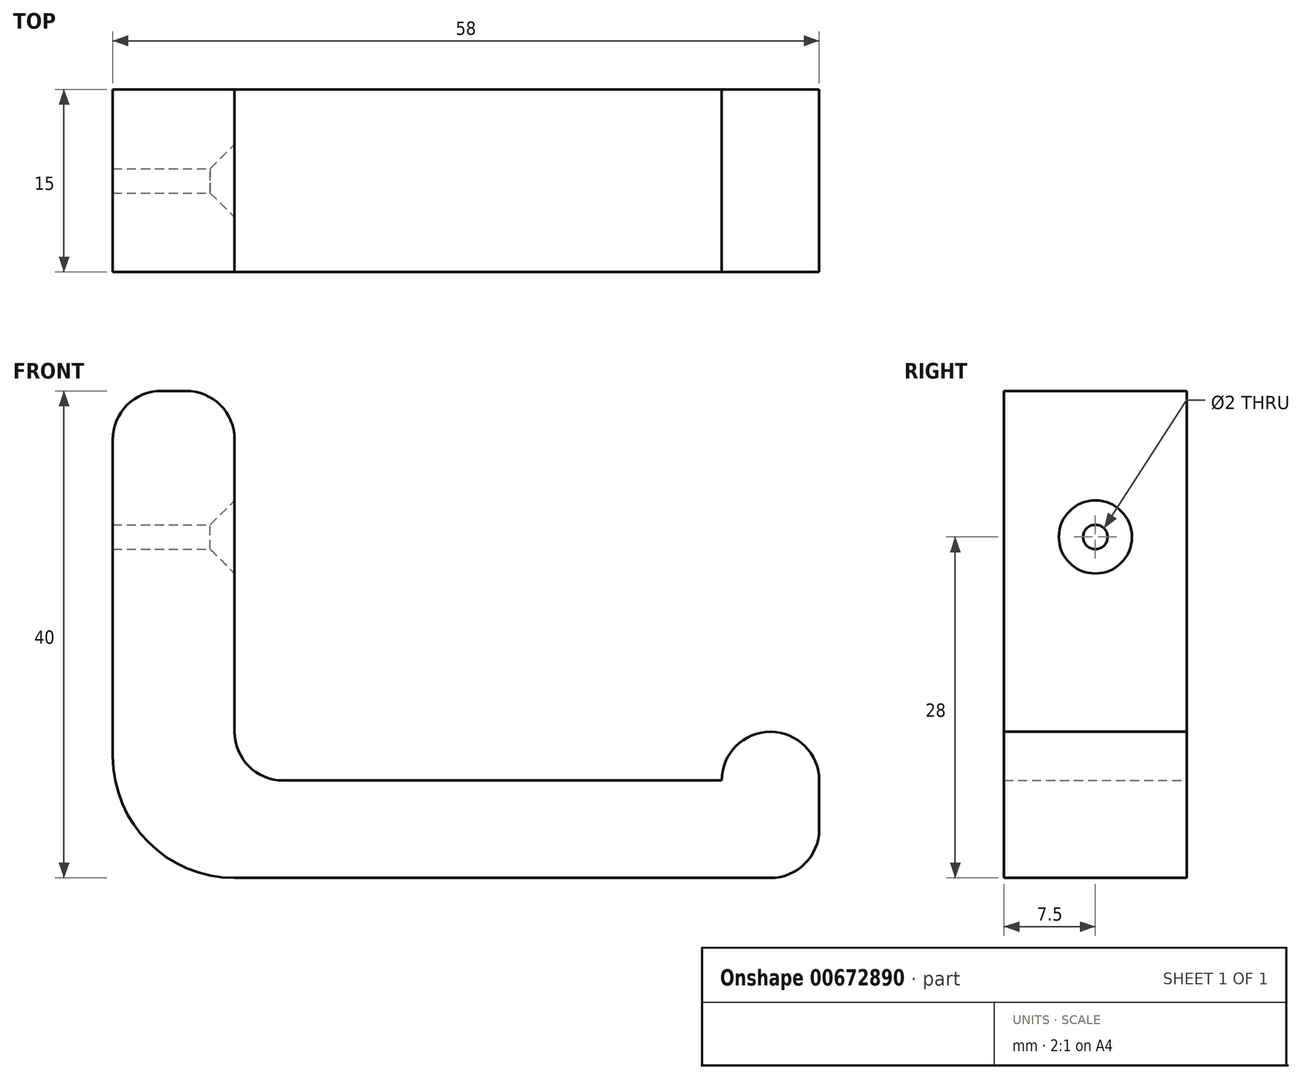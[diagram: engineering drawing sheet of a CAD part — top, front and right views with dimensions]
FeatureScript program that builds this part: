
annotation { "Feature Type Name" : "Feature", "Feature Type Description" : "" }
export const myFeature = defineFeature(function(context is Context, id is Id, definition is map)
    precondition{}
    {
        {
            var Q0;
            Q0=qCreatedBy(makeId("Front.planeOp"),FACE);
            var sketch = newSketch(context, id + "F0", { "sketchPlane" : qUnion([Q0])});
            skLineSegment(sketch, "E0.bottom", {"start": v(20, 4) * mm, "end": v(-20, 4) * mm});
            skLineSegment(sketch, "E0.top", {"start": v(20, -4) * mm, "end": v(-20, -4) * mm});
            skLineSegment(sketch, "E0.left", {"start": v(20, 4) * mm, "end": v(20, -4) * mm});
            skLineSegment(sketch, "E0.right", {"start": v(-20, 4) * mm, "end": v(-20, -4) * mm});
            skPoint(sketch, "E0.middle", {"position": v(0, 0) * mm});
            skLineSegment(sketch, "E1.bottom", {"start": v(-20, -4) * mm, "end": v(-30, -4) * mm});
            skLineSegment(sketch, "E1.top", {"start": v(-20, 36) * mm, "end": v(-30, 36) * mm});
            skLineSegment(sketch, "E1.left", {"start": v(-20, -4) * mm, "end": v(-20, 36) * mm});
            skLineSegment(sketch, "E1.right", {"start": v(-30, -4) * mm, "end": v(-30, 36) * mm});
            skLineSegment(sketch, "E2.bottom", {"start": v(20, -4) * mm, "end": v(28, -4) * mm});
            skLineSegment(sketch, "E2.top", {"start": v(20, 8) * mm, "end": v(28, 8) * mm});
            skLineSegment(sketch, "E2.left", {"start": v(20, -4) * mm, "end": v(20, 8) * mm});
            skLineSegment(sketch, "E2.right", {"start": v(28, -4) * mm, "end": v(28, 8) * mm});
            skSolve(sketch);
        }
        {
            var Q0;
            {var subQ3=sQuery(id+"F0.wireOp",EDGE,"E1.bottom");Q0=makeQuery(id+"F0.imprint","IMPRINT",FACE,{"disambiguationData":[TD([[makeQuery(id+"F0.imprint","IMPRINT",EDGE,{"derivedFrom":subQ3}),-1.0]])]});}
            var Q1;
            {var subQ0=sQuery(id+"F0.wireOp",EDGE,"E0.bottom");Q1=makeQuery(id+"F0.imprint","IMPRINT",FACE,{"disambiguationData":[TD([[makeQuery(id+"F0.imprint","IMPRINT",EDGE,{"derivedFrom":subQ0}),1.0]])]});}
            var Q2;
            {var subQ3=sQuery(id+"F0.wireOp",EDGE,"E2.bottom");Q2=makeQuery(id+"F0.imprint","IMPRINT",FACE,{"disambiguationData":[TD([[makeQuery(id+"F0.imprint","IMPRINT",EDGE,{"derivedFrom":subQ3}),1.0]])]});}
            extrude(context, id + "F1", {"entities" : qUnion([Q0, Q1, Q2]), "depth" : 15 * mm, "offsetDistance" : 25 * mm});
        }
        {
            var Q0;
            Q0=makeQuery(id+"F1.opExtrude","SWEPT_EDGE",EDGE,{"disambiguationData":[OSD([sQuery(id+"F0.wireOp",EDGE,"E0.bottom"),sQuery(id+"F0.wireOp",EDGE,"E1.left")])]});
            var Q1;
            Q1=makeQuery(id+"F1.opExtrude","SWEPT_EDGE",EDGE,{"disambiguationData":[OSD([sQuery(id+"F0.wireOp",EDGE,"E2.top"),sQuery(id+"F0.wireOp",EDGE,"E2.left")])]});
            var Q2;
            Q2=makeQuery(id+"F1.opExtrude","SWEPT_EDGE",EDGE,{"disambiguationData":[OSD([sQuery(id+"F0.wireOp",EDGE,"E2.top"),sQuery(id+"F0.wireOp",EDGE,"E2.right")])]});
            var Q3;
            Q3=makeQuery(id+"F1.opExtrude","SWEPT_EDGE",EDGE,{"disambiguationData":[OSD([sQuery(id+"F0.wireOp",EDGE,"E2.bottom"),sQuery(id+"F0.wireOp",EDGE,"E2.right")])]});
            var Q4;
            Q4=makeQuery(id+"F1.opExtrude","SWEPT_EDGE",EDGE,{"disambiguationData":[OSD([sQuery(id+"F0.wireOp",EDGE,"E1.top"),sQuery(id+"F0.wireOp",EDGE,"E1.left")])]});
            var Q5;
            Q5=makeQuery(id+"F1.opExtrude","SWEPT_EDGE",EDGE,{"disambiguationData":[OSD([sQuery(id+"F0.wireOp",EDGE,"E1.top"),sQuery(id+"F0.wireOp",EDGE,"E1.right")])]});
            fillet(context, id + "F2", {"entities" : qUnion([Q0, Q1, Q2, Q3, Q4, Q5]), "radius" : 4 * mm, "tangentPropagation" : true, "allowEdgeOverflow" : false});
        }
        {
            var Q0;
            Q0=makeQuery(id+"F1.opExtrude","SWEPT_EDGE",EDGE,{"disambiguationData":[OSD([sQuery(id+"F0.wireOp",EDGE,"E1.bottom"),sQuery(id+"F0.wireOp",EDGE,"E1.right")])]});
            fillet(context, id + "F3", {"entities" : qUnion([Q0]), "radius" : 10 * mm, "tangentPropagation" : true, "allowEdgeOverflow" : false});
        }
        {
            var Q0;
            Q0=makeQuery(id+"F1.opExtrude","SWEPT_FACE",FACE,{"disambiguationData":[OSD([sQuery(id+"F0.wireOp",EDGE,"E1.left")])]});
            var sketch = newSketch(context, id + "F4", { "sketchPlane" : qUnion([Q0])});
            skLineSegment(sketch, "E3", {"start": v(-15, 24) * mm, "end": v(0, 24) * mm});
            skCircle(sketch, "E4", {"center": v(-7.5, 24) * mm, "radius": 2.5 * mm});
            skSolve(sketch);
        }
        {
            var Q0;
            Q0=sQuery(id+"F4.wireOp",VERTEX,"E4.center");
            var Q1;
            Q1=makeQuery(id+"F1.opExtrude","SWEPT_BODY",BODY,{"disambiguationData":[OSD([sQuery(id+"F0.wireOp",EDGE,"E0.bottom"),sQuery(id+"F0.wireOp",EDGE,"E0.top"),sQuery(id+"F0.wireOp",EDGE,"E1.bottom"),sQuery(id+"F0.wireOp",EDGE,"E1.top"),sQuery(id+"F0.wireOp",EDGE,"E1.left"),sQuery(id+"F0.wireOp",EDGE,"E1.right"),sQuery(id+"F0.wireOp",EDGE,"E2.bottom"),sQuery(id+"F0.wireOp",EDGE,"E2.top"),sQuery(id+"F0.wireOp",EDGE,"E2.left"),sQuery(id+"F0.wireOp",EDGE,"E2.right")])]});
            hole(context, id + "F5", {"style" : HoleStyle.C_SINK, "endStyle" : HoleEndStyle.THROUGH, "holeDiameter" : 2 * mm, "cSinkDiameter" : 6 * mm, "cSinkAngle" : 90 * degree, "majorDiameter" : 5 * mm, "isTappedThrough" : true, "tappedDepth" : 12 * mm, "tapClearance" : 3, "locations" : qUnion([Q0]), "scope" : qUnion([Q1])});
        }
    });
